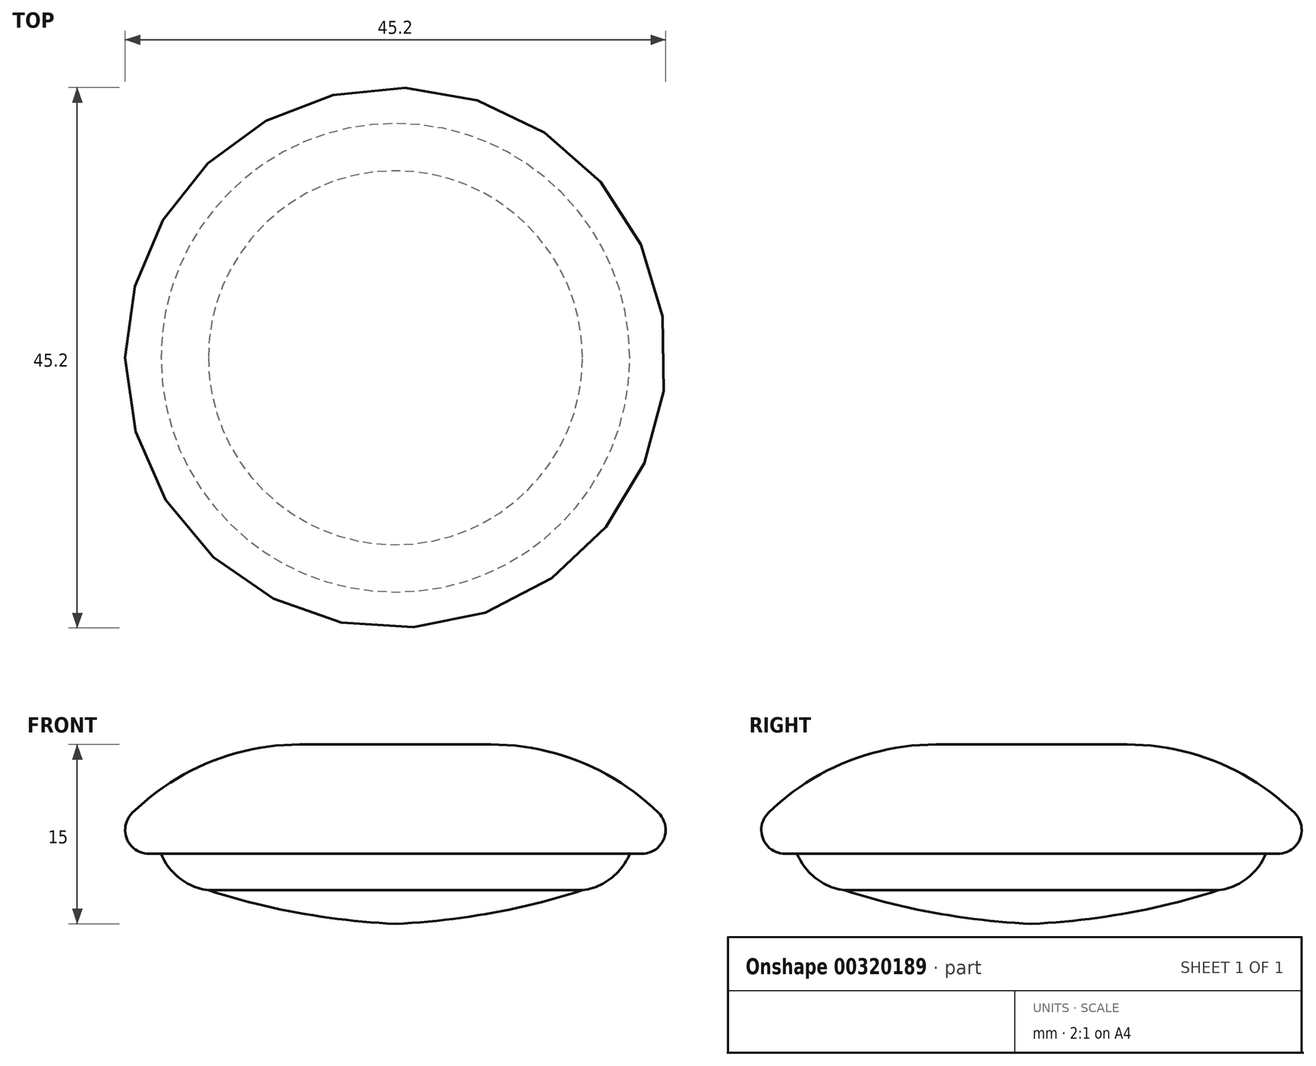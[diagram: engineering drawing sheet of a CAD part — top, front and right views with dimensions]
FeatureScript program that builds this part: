
annotation { "Feature Type Name" : "Feature", "Feature Type Description" : "" }
export const myFeature = defineFeature(function(context is Context, id is Id, definition is map)
    precondition{}
    {
        {
            var Q0;
            Q0=qCreatedBy(makeId("Front.planeOp"),FACE);
            var sketch = newSketch(context, id + "F0", { "sketchPlane" : qUnion([Q0])});
            skLineSegment(sketch, "E0", {"start": v(0, 0) * mm, "end": v(8, 0) * mm});
            skArc(sketch, "E1", {"start": v(22, -5.72) * mm, "mid": v(15.56, -1.48) * mm, "end": v(8, 0) * mm});
            skArc(sketch, "E2", {"start": v(20.6, -9.15) * mm, "mid": v(22.45, -7.9) * mm, "end": v(22, -5.72) * mm});
            skLineSegment(sketch, "E3", {"start": v(20.6, -9.15) * mm, "end": v(19.6, -9.15) * mm});
            skArc(sketch, "E4", {"start": v(15.64, -12.2) * mm, "mid": v(18.03, -11.2) * mm, "end": v(19.6, -9.15) * mm});
            skArc(sketch, "E5", {"start": v(0, -15) * mm, "mid": v(7.91, -14.12) * mm, "end": v(15.64, -12.2) * mm});
            skLineSegment(sketch, "E6", {"start": v(0, -15) * mm, "end": v(0, 0) * mm});
            skSolve(sketch);
        }
        {
            var Q0;
            Q0 = qSketchRegion(id + "F0", true);
            var Q1;
            Q1=sQuery(id+"F0.wireOp",EDGE,"E6");
            revolve(context, id + "F1", {"entities" : qUnion([Q0]), "axis" : qUnion([Q1]), "revolveType" : RevolveType.FULL});
        }
    });
